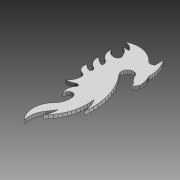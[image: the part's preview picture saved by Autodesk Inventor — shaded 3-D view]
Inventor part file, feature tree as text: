
AUTODESK INVENTOR PART (.ipt)
format: ipt  version: 2018 (Build 220112000, 112)  size: 707,584 bytes
history: native  units: mm
features: other x2, extrude x2, sketch x2
ambient origin geometry x8: Origin, YZ Plane, XZ Plane, XY Plane, X Axis, Y Axis, Z Axis, Center Point
bodies: Body1 (feature_tree)
feature tree (6):
  other  "ソリッド1"
  extrude  "押し出し1"  Depth=2.0mm TaperAngle=0.0deg
  extrude  "押し出し2"  Depth=10.0mm TaperAngle=0.0deg
  sketch  "スケッチ2"
  sketch  "スケッチ3"
  other  "断面エッジを投影1"
